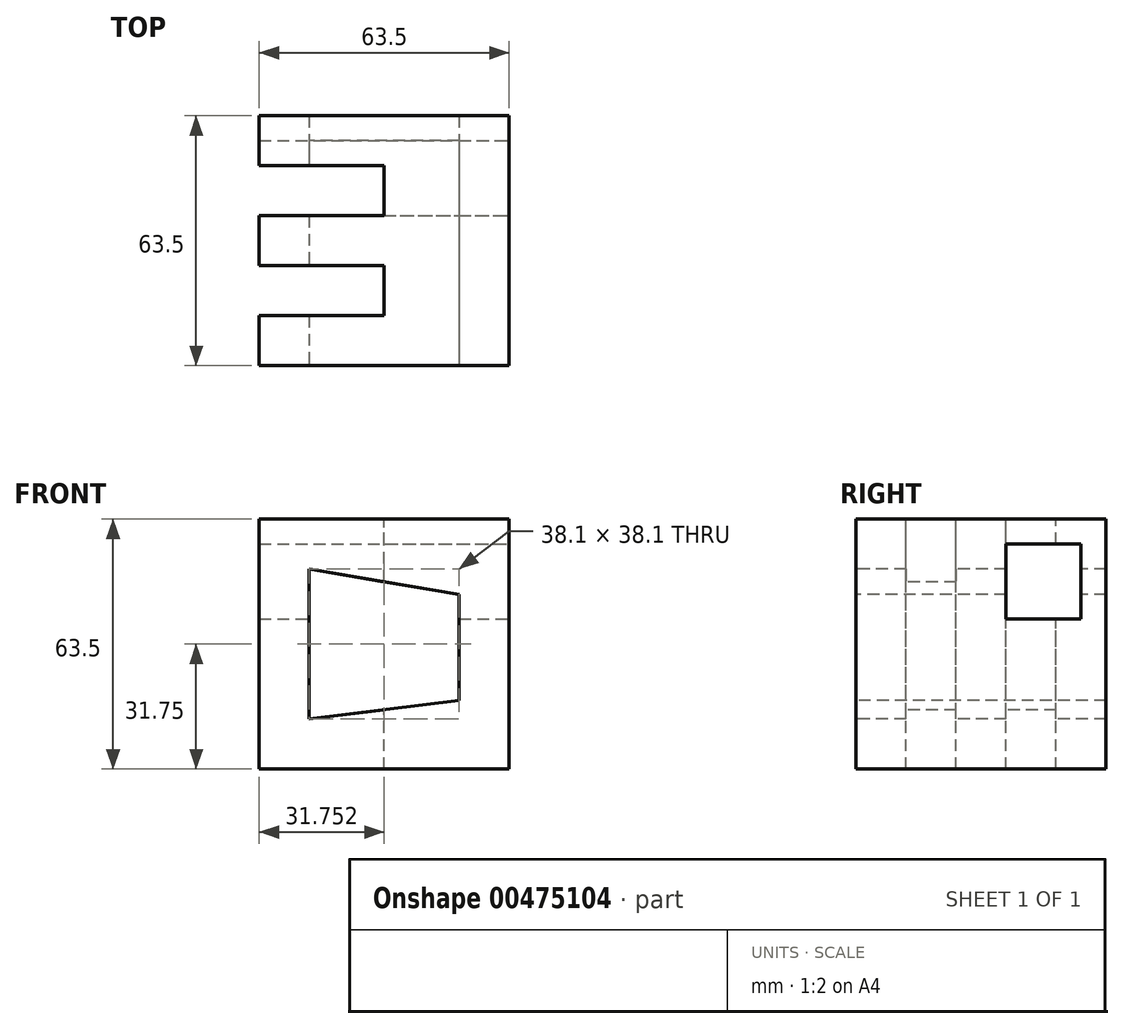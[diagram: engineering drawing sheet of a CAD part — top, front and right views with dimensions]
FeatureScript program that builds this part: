
annotation { "Feature Type Name" : "Feature", "Feature Type Description" : "" }
export const myFeature = defineFeature(function(context is Context, id is Id, definition is map)
    precondition{}
    {
        {
            var Q0;
            Q0=qCreatedBy(makeId("Top.planeOp"),FACE);
            var sketch = newSketch(context, id + "F0", { "sketchPlane" : qUnion([Q0])});
            skLineSegment(sketch, "E0.bottom", {"start": v(-60.25, -66.5) * mm, "end": v(3.25, -66.5) * mm});
            skLineSegment(sketch, "E0.top", {"start": v(-60.25, -3) * mm, "end": v(3.25, -3) * mm});
            skLineSegment(sketch, "E0.left", {"start": v(-60.25, -66.5) * mm, "end": v(-60.25, -3) * mm});
            skLineSegment(sketch, "E0.right", {"start": v(3.25, -66.5) * mm, "end": v(3.25, -3) * mm});
            skSolve(sketch);
        }
        {
            var Q0;
            Q0=makeQuery(id+"F0.imprint","IMPRINT",FACE,{"disambiguationData":[TD([[makeQuery(id+"F0.imprint","IMPRINT",EDGE,{"derivedFrom":sQuery(id+"F0.wireOp",EDGE,"E0.bottom")}),1.0]])]});
            extrude(context, id + "F1", {"entities" : qUnion([Q0]), "depth" : 63.5 * mm});
        }
        {
            var Q0;
            Q0=makeQuery(id+"F1.opExtrude","CAP_FACE",FACE,{"disambiguationData":[OSD([sQuery(id+"F0.wireOp",EDGE,"E0.bottom"),sQuery(id+"F0.wireOp",EDGE,"E0.top"),sQuery(id+"F0.wireOp",EDGE,"E0.left"),sQuery(id+"F0.wireOp",EDGE,"E0.right")])],"isStart":false});
            var sketch = newSketch(context, id + "F2", { "sketchPlane" : qUnion([Q0])});
            skLineSegment(sketch, "E1.bottom", {"start": v(-60.25, -66.5) * mm, "end": v(3.25, -66.5) * mm});
            skLineSegment(sketch, "E1.top", {"start": v(-60.25, -53.8) * mm, "end": v(3.25, -53.8) * mm});
            skLineSegment(sketch, "E1.left", {"start": v(-60.25, -66.5) * mm, "end": v(-60.25, -53.8) * mm});
            skLineSegment(sketch, "E1.right", {"start": v(3.25, -66.5) * mm, "end": v(3.25, -53.8) * mm});
            skLineSegment(sketch, "E2.top", {"start": v(-60.25, -41.1) * mm, "end": v(3.25, -41.1) * mm});
            skLineSegment(sketch, "E2.left", {"start": v(-60.25, -53.8) * mm, "end": v(-60.25, -41.1) * mm});
            skLineSegment(sketch, "E2.right", {"start": v(3.25, -53.8) * mm, "end": v(3.25, -41.1) * mm});
            skLineSegment(sketch, "E3.top", {"start": v(-60.25, -28.4) * mm, "end": v(3.25, -28.4) * mm});
            skLineSegment(sketch, "E3.left", {"start": v(-60.25, -41.1) * mm, "end": v(-60.25, -28.4) * mm});
            skLineSegment(sketch, "E3.right", {"start": v(3.25, -41.1) * mm, "end": v(3.25, -28.4) * mm});
            skLineSegment(sketch, "E4.top", {"start": v(-60.25, -15.7) * mm, "end": v(3.25, -15.7) * mm});
            skLineSegment(sketch, "E4.left", {"start": v(-60.25, -28.4) * mm, "end": v(-60.25, -15.7) * mm});
            skLineSegment(sketch, "E4.right", {"start": v(3.25, -28.4) * mm, "end": v(3.25, -15.7) * mm});
            skLineSegment(sketch, "E5", {"start": v(-28.5, -3) * mm, "end": v(-28.5, -66.5) * mm});
            skSolve(sketch);
        }
        {
            var Q0;
            {var subQ0=sQuery(id+"F2.wireOp",EDGE,"E2.left");Q0=makeQuery(id+"F2.imprint","IMPRINT",FACE,{"disambiguationData":[TD([[makeQuery(id+"F2.imprint","IMPRINT",EDGE,{"derivedFrom":subQ0}),-1.0]])]});}
            var Q1;
            {var subQ0=sQuery(id+"F2.wireOp",EDGE,"E4.left");Q1=makeQuery(id+"F2.imprint","IMPRINT",FACE,{"disambiguationData":[TD([[makeQuery(id+"F2.imprint","IMPRINT",EDGE,{"derivedFrom":subQ0}),-1.0]])]});}
            extrude(context, id + "F3", {"entities" : qUnion([Q0, Q1]), "operationType" : NewBodyOperationType.REMOVE, "oppositeDirection" : true, "depth" : 63.5 * mm});
        }
        {
            var Q0;
            Q0=makeQuery(id+"F1.opExtrude","SWEPT_FACE",FACE,{"disambiguationData":[OSD([sQuery(id+"F0.wireOp",EDGE,"E0.right")])]});
            var sketch = newSketch(context, id + "F4", { "sketchPlane" : qUnion([Q0])});
            skLineSegment(sketch, "E6", {"start": v(-34.74, 63.5) * mm, "end": v(-34.74, 0) * mm});
            skLineSegment(sketch, "E7", {"start": v(-66.5, 31.75) * mm, "end": v(-3, 31.75) * mm});
            skLineSegment(sketch, "E8.bottom", {"start": v(-34.74, 31.75) * mm, "end": v(-28.4, 31.75) * mm});
            skLineSegment(sketch, "E8.top", {"start": v(-34.74, 38.1) * mm, "end": v(-28.4, 38.1) * mm});
            skLineSegment(sketch, "E8.left", {"start": v(-34.74, 31.75) * mm, "end": v(-34.74, 38.1) * mm});
            skLineSegment(sketch, "E8.right", {"start": v(-28.4, 31.75) * mm, "end": v(-28.4, 38.1) * mm});
            skLineSegment(sketch, "E9.bottom", {"start": v(-3, 63.5) * mm, "end": v(-9.34, 63.5) * mm});
            skLineSegment(sketch, "E9.top", {"start": v(-3, 57.15) * mm, "end": v(-9.34, 57.15) * mm});
            skLineSegment(sketch, "E9.left", {"start": v(-3, 63.5) * mm, "end": v(-3, 57.15) * mm});
            skLineSegment(sketch, "E9.right", {"start": v(-9.34, 63.5) * mm, "end": v(-9.34, 57.15) * mm});
            skLineSegment(sketch, "E10.bottom", {"start": v(-28.4, 38.1) * mm, "end": v(-9.34, 38.1) * mm});
            skLineSegment(sketch, "E10.top", {"start": v(-28.4, 57.15) * mm, "end": v(-9.34, 57.15) * mm});
            skLineSegment(sketch, "E10.left", {"start": v(-28.4, 38.1) * mm, "end": v(-28.4, 57.15) * mm});
            skLineSegment(sketch, "E10.right", {"start": v(-9.34, 38.1) * mm, "end": v(-9.34, 57.15) * mm});
            skSolve(sketch);
        }
        {
            var Q0;
            {var subQ0=sQuery(id+"F4.wireOp",EDGE,"E8.bottom");Q0=makeQuery(id+"F4.imprint","IMPRINT",FACE,{"disambiguationData":[TD([[makeQuery(id+"F4.imprint","IMPRINT",EDGE,{"derivedFrom":subQ0}),-1.0]])]});}
            var Q1;
            Q1=makeQuery(id+"F4.imprint","IMPRINT",FACE,{"disambiguationData":[TD([[makeQuery(id+"F4.imprint","IMPRINT",EDGE,{"derivedFrom":sQuery(id+"F4.wireOp",EDGE,"E10.bottom")}),1.0]])]});
            extrude(context, id + "F5", {"entities" : qUnion([Q0, Q1]), "operationType" : NewBodyOperationType.REMOVE, "oppositeDirection" : true, "depth" : 63.5 * mm});
        }
        {
            var Q0;
            Q0=makeQuery(id+"F1.opExtrude","SWEPT_FACE",FACE,{"disambiguationData":[OSD([sQuery(id+"F0.wireOp",EDGE,"E0.bottom")])]});
            var sketch = newSketch(context, id + "F6", { "sketchPlane" : qUnion([Q0])});
            skLineSegment(sketch, "E11.bottom", {"start": v(-60.25, 0) * mm, "end": v(-47.55, 0) * mm});
            skLineSegment(sketch, "E11.top", {"start": v(-60.25, 12.7) * mm, "end": v(-47.55, 12.7) * mm});
            skLineSegment(sketch, "E11.left", {"start": v(-60.25, 0) * mm, "end": v(-60.25, 12.7) * mm});
            skLineSegment(sketch, "E11.right", {"start": v(-47.55, 0) * mm, "end": v(-47.55, 12.7) * mm});
            skLineSegment(sketch, "E12.bottom", {"start": v(3.25, 63.5) * mm, "end": v(-9.45, 63.5) * mm});
            skLineSegment(sketch, "E12.top", {"start": v(3.25, 50.8) * mm, "end": v(-9.45, 50.8) * mm});
            skLineSegment(sketch, "E12.left", {"start": v(3.25, 63.5) * mm, "end": v(3.25, 50.8) * mm});
            skLineSegment(sketch, "E12.right", {"start": v(-9.45, 63.5) * mm, "end": v(-9.45, 50.8) * mm});
            skLineSegment(sketch, "E13.bottom", {"start": v(-47.55, 12.7) * mm, "end": v(-9.45, 12.7) * mm});
            skLineSegment(sketch, "E13.top", {"start": v(-47.55, 50.8) * mm, "end": v(-9.45, 50.8) * mm});
            skLineSegment(sketch, "E13.left", {"start": v(-47.55, 12.7) * mm, "end": v(-47.55, 50.8) * mm});
            skLineSegment(sketch, "E13.right", {"start": v(-9.45, 12.7) * mm, "end": v(-9.45, 50.8) * mm});
            skLineSegment(sketch, "E14", {"start": v(-47.55, 50.8) * mm, "end": v(-9.45, 44.42) * mm});
            skLineSegment(sketch, "E15", {"start": v(-47.55, 12.7) * mm, "end": v(-9.45, 17.44) * mm});
            skSolve(sketch);
        }
        {
            var Q0;
            Q0=makeQuery(id+"F6.imprint","IMPRINT",FACE,{"disambiguationData":[TD([[makeQuery(id+"F6.imprint","IMPRINT",EDGE,{"derivedFrom":sQuery(id+"F6.wireOp",EDGE,"E13.left")}),-1.0]])]});
            extrude(context, id + "F7", {"entities" : qUnion([Q0]), "operationType" : NewBodyOperationType.REMOVE, "oppositeDirection" : true, "depth" : 63.5 * mm});
        }
    });
